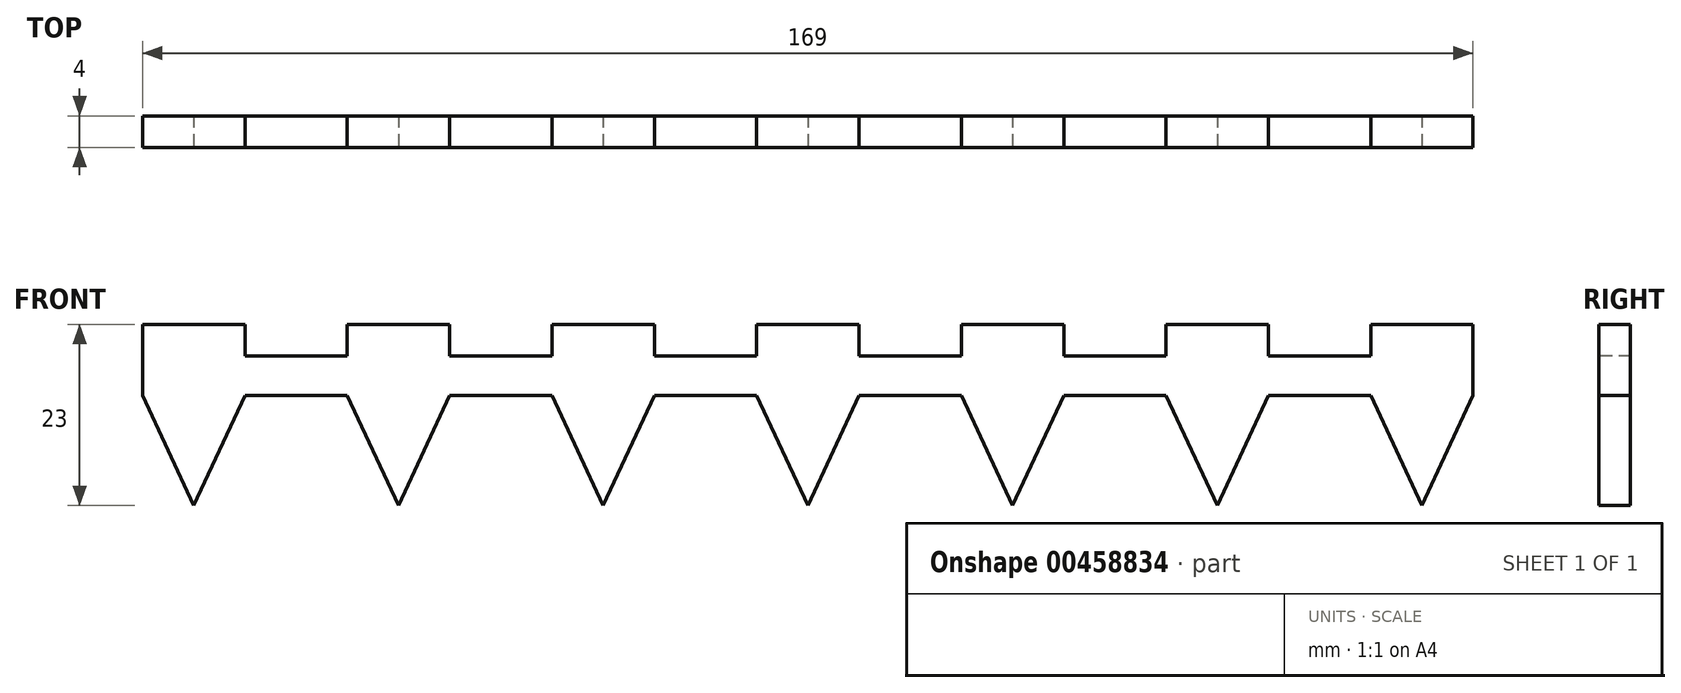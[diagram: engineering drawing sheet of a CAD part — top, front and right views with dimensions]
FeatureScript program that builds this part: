
annotation { "Feature Type Name" : "Feature", "Feature Type Description" : "" }
export const myFeature = defineFeature(function(context is Context, id is Id, definition is map)
    precondition{}
    {
        {
            var Q0;
            Q0=qCreatedBy(makeId("Top.planeOp"),FACE);
            var sketch = newSketch(context, id + "F0", { "sketchPlane" : qUnion([Q0])});
            skLineSegment(sketch, "E0.bottom", {"start": v(0, 0) * mm, "end": v(13, 0) * mm});
            skLineSegment(sketch, "E0.top", {"start": v(0, 4) * mm, "end": v(13, 4) * mm});
            skLineSegment(sketch, "E0.left", {"start": v(0, 0) * mm, "end": v(0, 4) * mm});
            skLineSegment(sketch, "E0.right", {"start": v(13, 0) * mm, "end": v(13, 4) * mm});
            skLineSegment(sketch, "E1.1.0.0", {"start": v(26, 4) * mm, "end": v(39, 4) * mm});
            skLineSegment(sketch, "E1.1.0.1", {"start": v(26, 0) * mm, "end": v(39, 0) * mm});
            skLineSegment(sketch, "E1.1.0.2", {"start": v(26, 0) * mm, "end": v(26, 4) * mm});
            skLineSegment(sketch, "E1.1.0.3", {"start": v(39, 0) * mm, "end": v(39, 4) * mm});
            skLineSegment(sketch, "E1.2.0.0", {"start": v(52, 4) * mm, "end": v(65, 4) * mm});
            skLineSegment(sketch, "E1.2.0.1", {"start": v(52, 0) * mm, "end": v(65, 0) * mm});
            skLineSegment(sketch, "E1.2.0.2", {"start": v(52, 0) * mm, "end": v(52, 4) * mm});
            skLineSegment(sketch, "E1.2.0.3", {"start": v(65, 0) * mm, "end": v(65, 4) * mm});
            skLineSegment(sketch, "E1.3.0.0", {"start": v(78, 4) * mm, "end": v(91, 4) * mm});
            skLineSegment(sketch, "E1.3.0.1", {"start": v(78, 0) * mm, "end": v(91, 0) * mm});
            skLineSegment(sketch, "E1.3.0.2", {"start": v(78, 0) * mm, "end": v(78, 4) * mm});
            skLineSegment(sketch, "E1.3.0.3", {"start": v(91, 0) * mm, "end": v(91, 4) * mm});
            skLineSegment(sketch, "E1.4.0.0", {"start": v(104, 4) * mm, "end": v(117, 4) * mm});
            skLineSegment(sketch, "E1.4.0.1", {"start": v(104, 0) * mm, "end": v(117, 0) * mm});
            skLineSegment(sketch, "E1.4.0.2", {"start": v(104, 0) * mm, "end": v(104, 4) * mm});
            skLineSegment(sketch, "E1.4.0.3", {"start": v(117, 0) * mm, "end": v(117, 4) * mm});
            skLineSegment(sketch, "E1.5.0.0", {"start": v(130, 4) * mm, "end": v(143, 4) * mm});
            skLineSegment(sketch, "E1.5.0.1", {"start": v(130, 0) * mm, "end": v(143, 0) * mm});
            skLineSegment(sketch, "E1.5.0.2", {"start": v(130, 0) * mm, "end": v(130, 4) * mm});
            skLineSegment(sketch, "E1.5.0.3", {"start": v(143, 0) * mm, "end": v(143, 4) * mm});
            skLineSegment(sketch, "E1.direction1", {"start": v(0, 0) * mm, "end": v(26, 0) * mm, "construction": true});
            skLineSegment(sketch, "E2.bottom", {"start": v(0, 4) * mm, "end": v(143, 4) * mm});
            skLineSegment(sketch, "E2.top", {"start": v(0, 0) * mm, "end": v(143, 0) * mm});
            skLineSegment(sketch, "E2.left", {"start": v(0, 4) * mm, "end": v(0, 0) * mm});
            skLineSegment(sketch, "E2.right", {"start": v(143, 4) * mm, "end": v(143, 0) * mm});
            skLineSegment(sketch, "E3.0.6.0", {"start": v(156, 4) * mm, "end": v(169, 4) * mm});
            skLineSegment(sketch, "E3.3.6.0", {"start": v(156, 0) * mm, "end": v(169, 0) * mm});
            skLineSegment(sketch, "E3.6.6.0", {"start": v(156, 0) * mm, "end": v(156, 4) * mm});
            skLineSegment(sketch, "E3.9.6.0", {"start": v(169, 0) * mm, "end": v(169, 4) * mm});
            skLineSegment(sketch, "E4", {"start": v(143, 4) * mm, "end": v(156, 4) * mm});
            skLineSegment(sketch, "E5", {"start": v(143, 0) * mm, "end": v(156, 0) * mm});
            skSolve(sketch);
        }
        {
            var Q0;
            Q0=qSketchRegion(id+"F0",true);
            extrude(context, id + "F1", {"entities" : qUnion([Q0]), "depth" : 5 * mm, "offsetDistance" : 25 * mm});
        }
        {
            var Q0;
            {var subQ0=sQuery(id+"F0.wireOp",EDGE,"E0.right");Q0=makeQuery(id+"F0.imprint","IMPRINT",FACE,{"disambiguationData":[TD([[makeQuery(id+"F0.imprint","IMPRINT",EDGE,{"derivedFrom":subQ0}),1.0]])]});}
            var Q1;
            {var subQ0=sQuery(id+"F0.wireOp",EDGE,"E1.1.0.2");Q1=makeQuery(id+"F0.imprint","IMPRINT",FACE,{"disambiguationData":[TD([[makeQuery(id+"F0.imprint","IMPRINT",EDGE,{"derivedFrom":subQ0}),-1.0]])]});}
            var Q2;
            {var subQ0=sQuery(id+"F0.wireOp",EDGE,"E1.2.0.2");Q2=makeQuery(id+"F0.imprint","IMPRINT",FACE,{"disambiguationData":[TD([[makeQuery(id+"F0.imprint","IMPRINT",EDGE,{"derivedFrom":subQ0}),-1.0]])]});}
            var Q3;
            {var subQ0=sQuery(id+"F0.wireOp",EDGE,"E1.3.0.2");Q3=makeQuery(id+"F0.imprint","IMPRINT",FACE,{"disambiguationData":[TD([[makeQuery(id+"F0.imprint","IMPRINT",EDGE,{"derivedFrom":subQ0}),-1.0]])]});}
            var Q4;
            {var subQ0=sQuery(id+"F0.wireOp",EDGE,"E1.4.0.2");Q4=makeQuery(id+"F0.imprint","IMPRINT",FACE,{"disambiguationData":[TD([[makeQuery(id+"F0.imprint","IMPRINT",EDGE,{"derivedFrom":subQ0}),-1.0]])]});}
            var Q5;
            {var subQ0=sQuery(id+"F0.wireOp",EDGE,"E1.5.0.2");Q5=makeQuery(id+"F0.imprint","IMPRINT",FACE,{"disambiguationData":[TD([[makeQuery(id+"F0.imprint","IMPRINT",EDGE,{"derivedFrom":subQ0}),-1.0]])]});}
            var Q6;
            Q6=makeQuery(id+"F0.imprint","IMPRINT",FACE,{"disambiguationData":[TD([[makeQuery(id+"F0.imprint","IMPRINT",EDGE,{"derivedFrom":sQuery(id+"F0.wireOp",EDGE,"E3.0.6.0")}),-1.0]])]});
            extrude(context, id + "F2", {"entities" : qUnion([Q0, Q1, Q2, Q3, Q4, Q5, Q6]), "operationType" : NewBodyOperationType.ADD, "depth" : 9 * mm, "offsetDistance" : 25 * mm});
        }
        {
            var Q0;
            {var subQ0=sQuery(id+"F0.wireOp",EDGE,"E2.top");Q0=makeQuery(id+"F2.boolean.opBoolean","MERGE",FACE,{"derivedFrom":[makeQuery(id+"F1.opExtrude","SWEPT_FACE",FACE,{"disambiguationData":[OSD([subQ0])]}),makeQuery(id+"F2.opExtrude","SWEPT_FACE",FACE,{"disambiguationData":[OSD([subQ0]),TDD([makeQuery(id+"F0.imprint","IMPRINT",EDGE,{"disambiguationData":[TD([[makeQuery(id+"F0.imprint","INTERSECT",VERTEX,{"derivedFrom":[sQuery(id+"F0.wireOp",EDGE,"E0.right"),subQ0]}),1.0]])],"derivedFrom":subQ0})])]}),makeQuery(id+"F2.opExtrude","SWEPT_FACE",FACE,{"disambiguationData":[OSD([subQ0]),TDD([makeQuery(id+"F0.imprint","IMPRINT",EDGE,{"disambiguationData":[TD([[makeQuery(id+"F0.imprint","INTERSECT",VERTEX,{"derivedFrom":[sQuery(id+"F0.wireOp",EDGE,"E1.1.0.2"),subQ0]}),-1.0]])],"derivedFrom":subQ0})])]}),makeQuery(id+"F2.opExtrude","SWEPT_FACE",FACE,{"disambiguationData":[OSD([subQ0]),TDD([makeQuery(id+"F0.imprint","IMPRINT",EDGE,{"disambiguationData":[TD([[makeQuery(id+"F0.imprint","INTERSECT",VERTEX,{"derivedFrom":[sQuery(id+"F0.wireOp",EDGE,"E1.2.0.2"),subQ0]}),-1.0]])],"derivedFrom":subQ0})])]}),makeQuery(id+"F2.opExtrude","SWEPT_FACE",FACE,{"disambiguationData":[OSD([subQ0]),TDD([makeQuery(id+"F0.imprint","IMPRINT",EDGE,{"disambiguationData":[TD([[makeQuery(id+"F0.imprint","INTERSECT",VERTEX,{"derivedFrom":[sQuery(id+"F0.wireOp",EDGE,"E1.3.0.2"),subQ0]}),-1.0]])],"derivedFrom":subQ0})])]}),makeQuery(id+"F2.opExtrude","SWEPT_FACE",FACE,{"disambiguationData":[OSD([subQ0]),TDD([makeQuery(id+"F0.imprint","IMPRINT",EDGE,{"disambiguationData":[TD([[makeQuery(id+"F0.imprint","INTERSECT",VERTEX,{"derivedFrom":[sQuery(id+"F0.wireOp",EDGE,"E1.4.0.2"),subQ0]}),-1.0]])],"derivedFrom":subQ0})])]}),makeQuery(id+"F2.opExtrude","SWEPT_FACE",FACE,{"disambiguationData":[OSD([subQ0]),TDD([makeQuery(id+"F0.imprint","IMPRINT",EDGE,{"disambiguationData":[TD([[makeQuery(id+"F0.imprint","INTERSECT",VERTEX,{"derivedFrom":[sQuery(id+"F0.wireOp",EDGE,"E1.5.0.2"),subQ0]}),-1.0]])],"derivedFrom":subQ0})])]})]});}
            var sketch = newSketch(context, id + "F3", { "sketchPlane" : qUnion([Q0])});
            skPoint(sketch, "E6.0", {"position": v(0, 0) * mm});
            skPoint(sketch, "E7.0", {"position": v(13, 0) * mm});
            skPoint(sketch, "E8.0", {"position": v(26, 0) * mm});
            skPoint(sketch, "E9.0", {"position": v(39, 0) * mm});
            skPoint(sketch, "E10.0", {"position": v(52, 0) * mm});
            skPoint(sketch, "E11.0", {"position": v(65, 0) * mm});
            skPoint(sketch, "E12.0", {"position": v(78, 0) * mm});
            skPoint(sketch, "E13.0", {"position": v(91, 0) * mm});
            skPoint(sketch, "E14.0", {"position": v(104, 0) * mm});
            skPoint(sketch, "E15.0", {"position": v(117, 0) * mm});
            skPoint(sketch, "E16.0", {"position": v(130, 0) * mm});
            skPoint(sketch, "E17.0", {"position": v(143, 0) * mm});
            skLineSegment(sketch, "E18", {"start": v(0, 0) * mm, "end": v(6.5, -14) * mm});
            skLineSegment(sketch, "E19", {"start": v(6.5, -14) * mm, "end": v(13, 0) * mm});
            skLineSegment(sketch, "E20", {"start": v(26, 0) * mm, "end": v(32.5, -14) * mm});
            skLineSegment(sketch, "E21", {"start": v(32.5, -14) * mm, "end": v(39, 0) * mm});
            skLineSegment(sketch, "E22", {"start": v(52, 0) * mm, "end": v(58.5, -14) * mm});
            skLineSegment(sketch, "E23", {"start": v(58.5, -14) * mm, "end": v(65, 0) * mm});
            skLineSegment(sketch, "E24", {"start": v(78, 0) * mm, "end": v(84.5, -14) * mm});
            skLineSegment(sketch, "E25", {"start": v(84.5, -14) * mm, "end": v(91, 0) * mm});
            skLineSegment(sketch, "E26", {"start": v(104, 0) * mm, "end": v(110.5, -14) * mm});
            skLineSegment(sketch, "E27", {"start": v(110.5, -14) * mm, "end": v(117, 0) * mm});
            skLineSegment(sketch, "E28", {"start": v(130, 0) * mm, "end": v(136.5, -14) * mm});
            skLineSegment(sketch, "E29", {"start": v(136.5, -14) * mm, "end": v(143, 0) * mm});
            skPoint(sketch, "E30.0", {"position": v(156, 0) * mm});
            skPoint(sketch, "E31.0", {"position": v(169, 0) * mm});
            skLineSegment(sketch, "E32", {"start": v(156, 0) * mm, "end": v(162.5, -14) * mm});
            skLineSegment(sketch, "E33", {"start": v(162.5, -14) * mm, "end": v(169, 0) * mm});
            skLineSegment(sketch, "E34", {"start": v(162.5, -14) * mm, "end": v(162.5, 0) * mm});
            skSolve(sketch);
        }
        {
            var Q0;
            {var subQ0=sQuery(id+"F3.wireOp",EDGE,"E18");Q0=makeQuery(id+"F3.imprint","IMPRINT",FACE,{"disambiguationData":[TD([[makeQuery(id+"F3.imprint","IMPRINT",EDGE,{"derivedFrom":subQ0}),1.0]])]});}
            var Q1;
            {var subQ0=sQuery(id+"F3.wireOp",EDGE,"E20");Q1=makeQuery(id+"F3.imprint","IMPRINT",FACE,{"disambiguationData":[TD([[makeQuery(id+"F3.imprint","IMPRINT",EDGE,{"derivedFrom":subQ0}),1.0]])]});}
            var Q2;
            {var subQ0=sQuery(id+"F3.wireOp",EDGE,"E22");Q2=makeQuery(id+"F3.imprint","IMPRINT",FACE,{"disambiguationData":[TD([[makeQuery(id+"F3.imprint","IMPRINT",EDGE,{"derivedFrom":subQ0}),1.0]])]});}
            var Q3;
            {var subQ0=sQuery(id+"F3.wireOp",EDGE,"E24");Q3=makeQuery(id+"F3.imprint","IMPRINT",FACE,{"disambiguationData":[TD([[makeQuery(id+"F3.imprint","IMPRINT",EDGE,{"derivedFrom":subQ0}),1.0]])]});}
            var Q4;
            {var subQ0=sQuery(id+"F3.wireOp",EDGE,"E26");Q4=makeQuery(id+"F3.imprint","IMPRINT",FACE,{"disambiguationData":[TD([[makeQuery(id+"F3.imprint","IMPRINT",EDGE,{"derivedFrom":subQ0}),1.0]])]});}
            var Q5;
            {var subQ0=sQuery(id+"F3.wireOp",EDGE,"E28");Q5=makeQuery(id+"F3.imprint","IMPRINT",FACE,{"disambiguationData":[TD([[makeQuery(id+"F3.imprint","IMPRINT",EDGE,{"derivedFrom":subQ0}),1.0]])]});}
            var Q6;
            {var subQ0=sQuery(id+"F3.wireOp",EDGE,"E32");Q6=makeQuery(id+"F3.imprint","IMPRINT",FACE,{"disambiguationData":[TD([[makeQuery(id+"F3.imprint","IMPRINT",EDGE,{"derivedFrom":subQ0}),1.0]])]});}
            var Q7;
            {var subQ0=sQuery(id+"F3.wireOp",EDGE,"E33");Q7=makeQuery(id+"F3.imprint","IMPRINT",FACE,{"disambiguationData":[TD([[makeQuery(id+"F3.imprint","IMPRINT",EDGE,{"derivedFrom":subQ0}),1.0]])]});}
            extrude(context, id + "F4", {"entities" : qUnion([Q0, Q1, Q2, Q3, Q4, Q5, Q6, Q7]), "operationType" : NewBodyOperationType.ADD, "oppositeDirection" : true, "depth" : 4 * mm, "offsetDistance" : 25 * mm});
        }
    });
